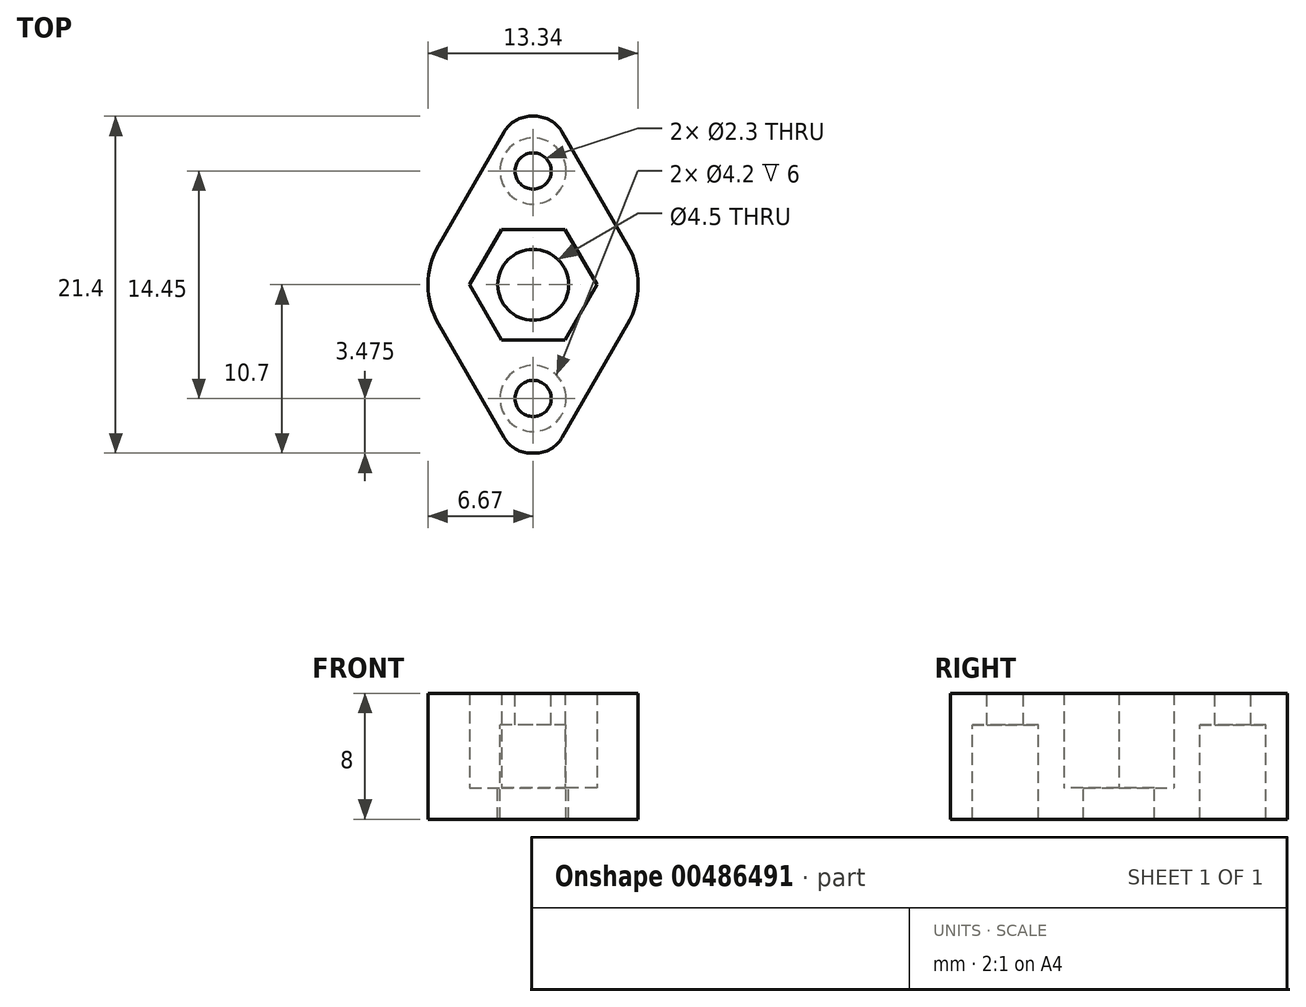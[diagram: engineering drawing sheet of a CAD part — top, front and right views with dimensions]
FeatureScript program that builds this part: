
annotation { "Feature Type Name" : "Feature", "Feature Type Description" : "" }
export const myFeature = defineFeature(function(context is Context, id is Id, definition is map)
    precondition{}
    {
        {
            var Q0;
            Q0=qCreatedBy(makeId("Top.planeOp"),FACE);
            var sketch = newSketch(context, id + "F0", { "sketchPlane" : qUnion([Q0])});
            skLineSegment(sketch, "E0", {"start": v(0, 3.45) * mm, "end": v(-2, 3.45) * mm});
            skLineSegment(sketch, "E1", {"start": v(-2, 3.45) * mm, "end": v(-3.98, 0) * mm});
            skLineSegment(sketch, "E2", {"start": v(0, 0) * mm, "end": v(-2.43, -4.2) * mm, "construction": true});
            skLineSegment(sketch, "E3.MirrorCS", {"start": v(2, 3.45) * mm, "end": v(3.98, 0) * mm});
            skLineSegment(sketch, "E4.MirrorCS", {"start": v(0, 3.45) * mm, "end": v(2, 3.45) * mm});
            skLineSegment(sketch, "E5.MirrorCS", {"start": v(-2, -3.45) * mm, "end": v(-3.98, 0) * mm});
            skLineSegment(sketch, "E6.MirrorCS", {"start": v(0, -3.45) * mm, "end": v(-2, -3.45) * mm});
            skLineSegment(sketch, "E7.MirrorCS", {"start": v(0, -3.45) * mm, "end": v(2, -3.45) * mm});
            skLineSegment(sketch, "E8.MirrorCS", {"start": v(2, -3.45) * mm, "end": v(3.98, 0) * mm});
            skCircle(sketch, "E9", {"center": v(0, 7.22) * mm, "radius": 1.1 * mm});
            skCircle(sketch, "E10.MirrorC", {"center": v(0, -7.22) * mm, "radius": 1.1 * mm});
            skSolve(sketch);
        }
        {
            var Q0;
            Q0=qCreatedBy(makeId("Top.planeOp"),FACE);
            var sketch = newSketch(context, id + "F1", { "sketchPlane" : qUnion([Q0])});
            skLineSegment(sketch, "E11", {"start": v(0, 17.08) * mm, "end": v(4, 17.08) * mm});
            skLineSegment(sketch, "E12", {"start": v(0, 10.7) * mm, "end": v(1.27, 10.7) * mm});
            skLineSegment(sketch, "E13", {"start": v(1.27, 10.7) * mm, "end": v(7.45, 0) * mm});
            skLineSegment(sketch, "E14.MirrorCS", {"start": v(1.27, -10.7) * mm, "end": v(7.45, 0) * mm});
            skLineSegment(sketch, "E15.MirrorCS", {"start": v(0, -10.7) * mm, "end": v(1.27, -10.7) * mm});
            skLineSegment(sketch, "E16.MirrorCS", {"start": v(0, 10.7) * mm, "end": v(-1.27, 10.7) * mm});
            skLineSegment(sketch, "E17.MirrorCS", {"start": v(-1.27, 10.7) * mm, "end": v(-7.45, 0) * mm});
            skLineSegment(sketch, "E18.MirrorCS", {"start": v(-1.27, -10.7) * mm, "end": v(-7.45, 0) * mm});
            skLineSegment(sketch, "E19.MirrorCS", {"start": v(0, -10.7) * mm, "end": v(-1.27, -10.7) * mm});
            skSolve(sketch);
        }
        {
            var Q0;
            Q0=qSketchRegion(id+"F1",true);
            extrude(context, id + "F2", {"entities" : qUnion([Q0]), "oppositeDirection" : true, "depth" : 2 * mm, "offsetDistance" : 25 * mm});
        }
        {
            var Q0;
            Q0=qCreatedBy(makeId("Top.planeOp"),FACE);
            var sketch = newSketch(context, id + "F3", { "sketchPlane" : qUnion([Q0])});
            skCircle(sketch, "E20", {"center": v(0, 7.22) * mm, "radius": 1.15 * mm});
            skCircle(sketch, "E21.MirrorC", {"center": v(0, -7.22) * mm, "radius": 1.15 * mm});
            skSolve(sketch);
        }
        {
            var Q0;
            Q0=qCreatedBy(makeId("Top.planeOp"),FACE);
            var sketch = newSketch(context, id + "F4", { "sketchPlane" : qUnion([Q0])});
            skCircle(sketch, "E22", {"center": v(0, 7.22) * mm, "radius": 2.1 * mm});
            skCircle(sketch, "E23.MirrorC", {"center": v(0, -7.22) * mm, "radius": 2.1 * mm});
            skSolve(sketch);
        }
        {
            var Q0;
            Q0=qCreatedBy(makeId("Top.planeOp"),FACE);
            var sketch = newSketch(context, id + "F5", { "sketchPlane" : qUnion([Q0])});
            skLineSegment(sketch, "E24", {"start": v(4.04, 0) * mm, "end": v(2.02, 3.5) * mm});
            skLineSegment(sketch, "E25", {"start": v(2.02, 3.5) * mm, "end": v(0, 3.5) * mm});
            skLineSegment(sketch, "E26", {"start": v(7.45, 0) * mm, "end": v(1.27, 10.7) * mm});
            skLineSegment(sketch, "E27", {"start": v(0, 10.7) * mm, "end": v(1.27, 10.7) * mm});
            skLineSegment(sketch, "E28.MirrorCS", {"start": v(-7.45, 0) * mm, "end": v(-1.27, 10.7) * mm});
            skLineSegment(sketch, "E29.MirrorCS", {"start": v(0, 10.7) * mm, "end": v(-1.27, 10.7) * mm});
            skLineSegment(sketch, "E30.MirrorCS", {"start": v(-4.04, 0) * mm, "end": v(-2.02, 3.5) * mm});
            skLineSegment(sketch, "E31.MirrorCS", {"start": v(-2.02, 3.5) * mm, "end": v(0, 3.5) * mm});
            skLineSegment(sketch, "E32.MirrorCS", {"start": v(-2.02, -3.5) * mm, "end": v(0, -3.5) * mm});
            skLineSegment(sketch, "E33.MirrorCS", {"start": v(-4.04, 0) * mm, "end": v(-2.02, -3.5) * mm});
            skLineSegment(sketch, "E34.MirrorCS", {"start": v(0, -10.7) * mm, "end": v(-1.27, -10.7) * mm});
            skLineSegment(sketch, "E35.MirrorCS", {"start": v(-7.45, 0) * mm, "end": v(-1.27, -10.7) * mm});
            skLineSegment(sketch, "E36.MirrorCS", {"start": v(0, -10.7) * mm, "end": v(1.27, -10.7) * mm});
            skLineSegment(sketch, "E37.MirrorCS", {"start": v(4.04, 0) * mm, "end": v(2.02, -3.5) * mm});
            skLineSegment(sketch, "E38.MirrorCS", {"start": v(7.45, 0) * mm, "end": v(1.27, -10.7) * mm});
            skLineSegment(sketch, "E39.MirrorCS", {"start": v(2.02, -3.5) * mm, "end": v(0, -3.5) * mm});
            skSolve(sketch);
        }
        {
            var Q0;
            Q0=qCreatedBy(makeId("Top.planeOp"),FACE);
            var sketch = newSketch(context, id + "F6", { "sketchPlane" : qUnion([Q0])});
            skCircle(sketch, "E40", {"center": v(0, 0) * mm, "radius": 2.25 * mm});
            skSolve(sketch);
        }
        {
            var Q0;
            Q0=qSketchRegion(id+"F5",true);
            extrude(context, id + "F7", {"entities" : qUnion([Q0]), "operationType" : NewBodyOperationType.ADD, "depth" : 6 * mm, "offsetDistance" : 25 * mm});
        }
        {
            var Q0;
            Q0=qSketchRegion(id+"F3",true);
            extrude(context, id + "F8", {"entities" : qUnion([Q0]), "operationType" : NewBodyOperationType.REMOVE, "endBound" : BoundingType.THROUGH_ALL, "oppositeDirection" : true, "depth" : 25 * mm, "offsetDistance" : 25 * mm, "hasSecondDirection" : true, "secondDirectionBound" : BoundingType.THROUGH_ALL, "secondDirectionOppositeDirection" : false, "secondDirectionDepth" : 25 * mm});
        }
        {
            var Q0;
            Q0=qSketchRegion(id+"F4",true);
            extrude(context, id + "F9", {"entities" : qUnion([Q0]), "operationType" : NewBodyOperationType.REMOVE, "endBound" : BoundingType.THROUGH_ALL, "oppositeDirection" : true, "depth" : 25 * mm, "offsetDistance" : 25 * mm, "hasSecondDirection" : true, "secondDirectionOppositeDirection" : false, "secondDirectionDepth" : 4 * mm});
        }
        {
            var Q0;
            Q0=qSketchRegion(id+"F6",true);
            extrude(context, id + "F10", {"entities" : qUnion([Q0]), "operationType" : NewBodyOperationType.REMOVE, "endBound" : BoundingType.THROUGH_ALL, "oppositeDirection" : true, "depth" : 25 * mm, "offsetDistance" : 25 * mm});
        }
        {
            var Q0;
            Q0=makeQuery(id+"F7.boolean.opBoolean","MERGE",EDGE,{"derivedFrom":[makeQuery(id+"F2.opExtrude","SWEPT_EDGE",EDGE,{"disambiguationData":[OSD([sQuery(id+"F1.wireOp",EDGE,"E13"),sQuery(id+"F1.wireOp",EDGE,"E14.MirrorCS")])]}),makeQuery(id+"F7.opExtrude","SWEPT_EDGE",EDGE,{"disambiguationData":[OSD([sQuery(id+"F5.wireOp",EDGE,"E26"),sQuery(id+"F5.wireOp",EDGE,"E38.MirrorCS")])]})]});
            var Q1;
            Q1=makeQuery(id+"F7.boolean.opBoolean","MERGE",EDGE,{"derivedFrom":[makeQuery(id+"F2.opExtrude","SWEPT_EDGE",EDGE,{"disambiguationData":[OSD([sQuery(id+"F1.wireOp",EDGE,"E17.MirrorCS"),sQuery(id+"F1.wireOp",EDGE,"E18.MirrorCS")])]}),makeQuery(id+"F7.opExtrude","SWEPT_EDGE",EDGE,{"disambiguationData":[OSD([sQuery(id+"F5.wireOp",EDGE,"E28.MirrorCS"),sQuery(id+"F5.wireOp",EDGE,"E35.MirrorCS")])]})]});
            fillet(context, id + "F11", {"entities" : qUnion([Q0, Q1]), "radius" : 5 * mm, "tangentPropagation" : true, "allowEdgeOverflow" : false});
        }
        {
            var Q0;
            Q0=makeQuery(id+"F7.boolean.opBoolean","MERGE",EDGE,{"derivedFrom":[makeQuery(id+"F2.opExtrude","SWEPT_EDGE",EDGE,{"disambiguationData":[OSD([sQuery(id+"F1.wireOp",EDGE,"E14.MirrorCS"),sQuery(id+"F1.wireOp",EDGE,"E15.MirrorCS")])]}),makeQuery(id+"F7.opExtrude","SWEPT_EDGE",EDGE,{"disambiguationData":[OSD([sQuery(id+"F5.wireOp",EDGE,"E36.MirrorCS"),sQuery(id+"F5.wireOp",EDGE,"E38.MirrorCS")])]})]});
            var Q1;
            Q1=makeQuery(id+"F7.boolean.opBoolean","MERGE",EDGE,{"derivedFrom":[makeQuery(id+"F2.opExtrude","SWEPT_EDGE",EDGE,{"disambiguationData":[OSD([sQuery(id+"F1.wireOp",EDGE,"E18.MirrorCS"),sQuery(id+"F1.wireOp",EDGE,"E19.MirrorCS")])]}),makeQuery(id+"F7.opExtrude","SWEPT_EDGE",EDGE,{"disambiguationData":[OSD([sQuery(id+"F5.wireOp",EDGE,"E34.MirrorCS"),sQuery(id+"F5.wireOp",EDGE,"E35.MirrorCS")])]})]});
            var Q2;
            Q2=makeQuery(id+"F7.boolean.opBoolean","MERGE",EDGE,{"derivedFrom":[makeQuery(id+"F2.opExtrude","SWEPT_EDGE",EDGE,{"disambiguationData":[OSD([sQuery(id+"F1.wireOp",EDGE,"E16.MirrorCS"),sQuery(id+"F1.wireOp",EDGE,"E17.MirrorCS")])]}),makeQuery(id+"F7.opExtrude","SWEPT_EDGE",EDGE,{"disambiguationData":[OSD([sQuery(id+"F5.wireOp",EDGE,"E28.MirrorCS"),sQuery(id+"F5.wireOp",EDGE,"E29.MirrorCS")])]})]});
            var Q3;
            Q3=makeQuery(id+"F7.boolean.opBoolean","MERGE",EDGE,{"derivedFrom":[makeQuery(id+"F2.opExtrude","SWEPT_EDGE",EDGE,{"disambiguationData":[OSD([sQuery(id+"F1.wireOp",EDGE,"E12"),sQuery(id+"F1.wireOp",EDGE,"E13")])]}),makeQuery(id+"F7.opExtrude","SWEPT_EDGE",EDGE,{"disambiguationData":[OSD([sQuery(id+"F5.wireOp",EDGE,"E26"),sQuery(id+"F5.wireOp",EDGE,"E27")])]})]});
            fillet(context, id + "F12", {"entities" : qUnion([Q0, Q1, Q2, Q3]), "radius" : 2 * mm, "tangentPropagation" : true, "allowEdgeOverflow" : false});
        }
    });
